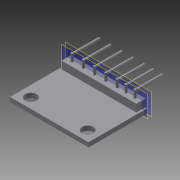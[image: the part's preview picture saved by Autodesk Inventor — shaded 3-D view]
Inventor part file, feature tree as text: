
AUTODESK INVENTOR PART (.ipt)
format: ipt  version: 2016 (Build 200138000, 138)  size: 164,352 bytes
history: native  units: in
note: dims shown in document units (in); Inventor stores cm internally (conversion verified against a paired STEP export)
features: extrude x4, sketch x4, plane x2
ambient origin geometry x8: Origin, YZ Plane, XZ Plane, XY Plane, X Axis, Y Axis, Z Axis, Center Point
bodies: Solid1 (feature_tree)
feature tree (10):
  extrude  "Extrusion1"  Depth=0.622in
  extrude  "Extrusion2"  Depth=0.1181in
  extrude  "Extrusion3"  Depth=0.1142in
  plane  "Work Plane2"
  extrude  "Extrusion4"  Depth=0.2953in
  sketch  "Sketch1"  dims[d0=0.8268in d1=0.622in]
  sketch  "Sketch2"  dims[d2=0.1181in d3=0.1181in]
  sketch  "Sketch3"  dims[d4=0.1142in d5=0.1142in]
  plane  "Work Plane1"
  sketch  "Sketch4"  dims[d6=0.1063in d7=0.1063in d8=0.0472in d9=0.0in d10=0.7874in d11=0.0984in d12=0.0in d13=0.0197in d14=0.0787in d15=0.0in d16=0.0236in d17=0.0236in d18=0.0236in d19=0.0236in d20=0.0236in d21=0.0236in d22=0.0236in d24=0.063in d25=0.1181in d26=0.1181in d27=0.1181in d28=0.1181in d29=0.1181in d30=0.1181in d31=0.0787in d32=0.0in d33=90.0deg d34=-0.0591in d37=0.0236in d38=0.0236in d39=0.0236in d40=0.0236in d41=0.0236in d42=0.0236in d43=0.0236in d44=0.2953in d45=0.0in]
